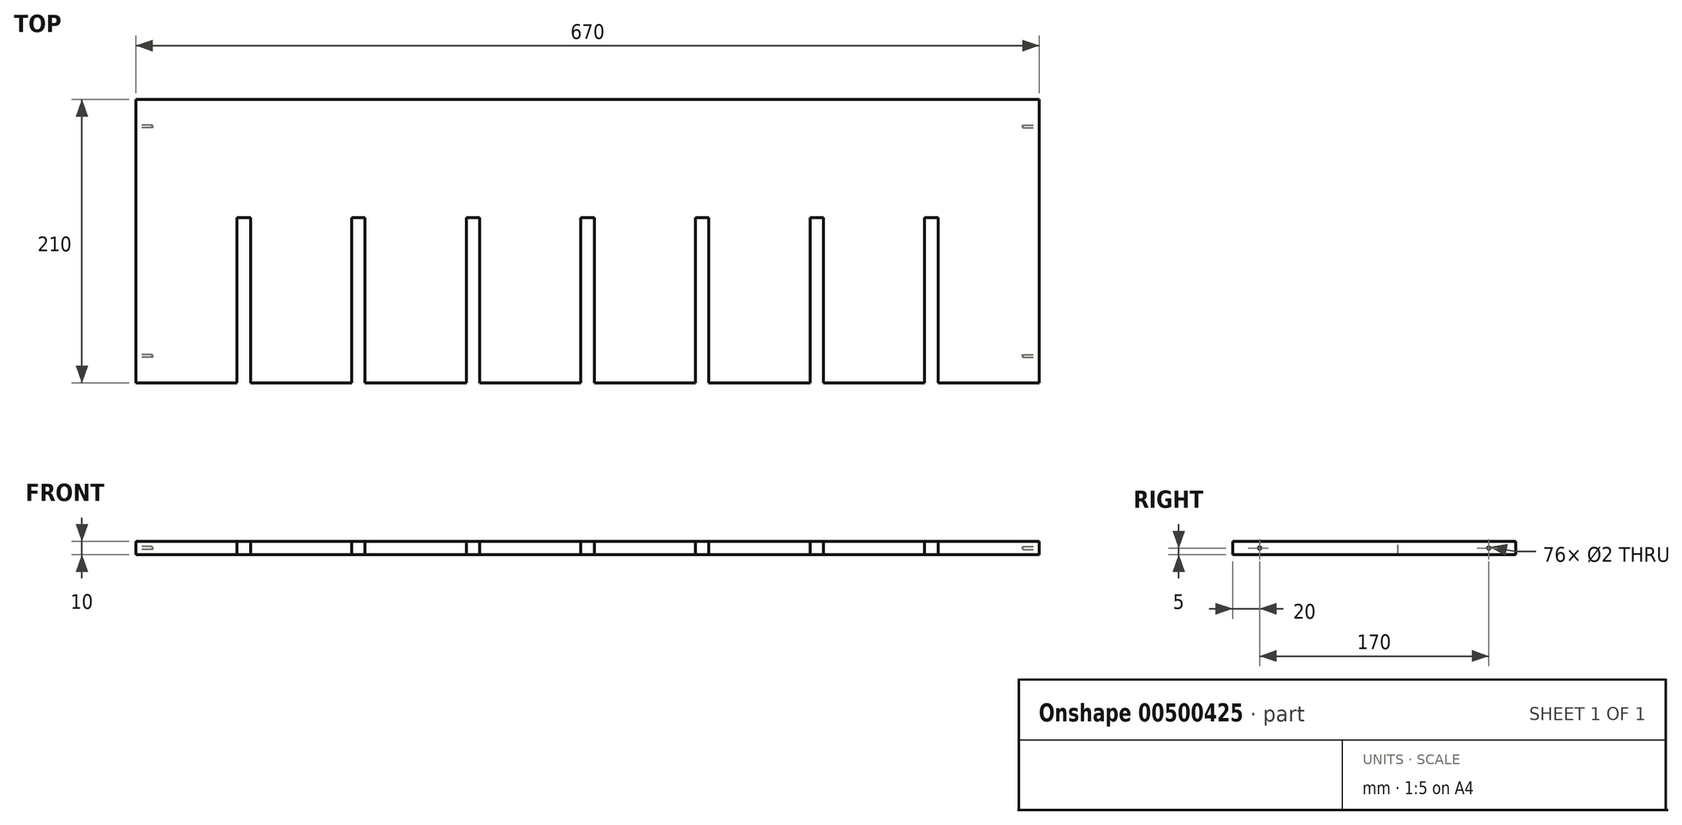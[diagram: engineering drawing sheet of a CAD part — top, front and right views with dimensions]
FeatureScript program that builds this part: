
annotation { "Feature Type Name" : "Feature", "Feature Type Description" : "" }
export const myFeature = defineFeature(function(context is Context, id is Id, definition is map)
    precondition{}
    {
        {
            var Q0;
            Q0=qCreatedBy(makeId("Top.planeOp"),FACE);
            var sketch = newSketch(context, id + "F0", { "sketchPlane" : qUnion([Q0])});
            skLineSegment(sketch, "E0.bottom", {"start": v(0, 0) * mm, "end": v(-670, 0) * mm});
            skLineSegment(sketch, "E0.top", {"start": v(0, 210) * mm, "end": v(-670, 210) * mm});
            skLineSegment(sketch, "E0.left", {"start": v(0, 0) * mm, "end": v(0, 210) * mm});
            skLineSegment(sketch, "E0.right", {"start": v(-670, 0) * mm, "end": v(-670, 210) * mm});
            skSolve(sketch);
        }
        {
            var Q0;
            Q0 = qSketchRegion(id + "F0", true);
            extrude(context, id + "F1", {"entities" : qUnion([Q0]), "depth" : 10 * mm});
        }
        {
            var Q0;
            Q0=makeQuery(id+"F1.opExtrude","CAP_FACE",FACE,{"disambiguationData":[OSD([sQuery(id+"F0.wireOp",EDGE,"E0.bottom"),sQuery(id+"F0.wireOp",EDGE,"E0.top"),sQuery(id+"F0.wireOp",EDGE,"E0.left"),sQuery(id+"F0.wireOp",EDGE,"E0.right")])],"isStart":false});
            var sketch = newSketch(context, id + "F2", { "sketchPlane" : qUnion([Q0])});
            skPoint(sketch, "E1", {"position": v(-595, 122.53) * mm});
            skPoint(sketch, "E2", {"position": v(-585, 122.53) * mm});
            skPoint(sketch, "E3", {"position": v(-510, 122.53) * mm});
            skPoint(sketch, "E4", {"position": v(-500, 122.53) * mm});
            skPoint(sketch, "E5", {"position": v(-425, 122.53) * mm});
            skPoint(sketch, "E6", {"position": v(-85, 122.53) * mm});
            skPoint(sketch, "E7", {"position": v(-75, 122.53) * mm});
            skPoint(sketch, "E8", {"position": v(-415, 122.53) * mm});
            skPoint(sketch, "E9", {"position": v(-340, 122.53) * mm});
            skPoint(sketch, "E10", {"position": v(-330, 122.53) * mm});
            skPoint(sketch, "E11", {"position": v(-255, 122.53) * mm});
            skPoint(sketch, "E12", {"position": v(-245, 122.53) * mm});
            skPoint(sketch, "E13", {"position": v(-170, 122.53) * mm});
            skPoint(sketch, "E14", {"position": v(-160, 122.53) * mm});
            skLineSegment(sketch, "E15.bottom", {"start": v(-595, 122.53) * mm, "end": v(-585, 122.53) * mm});
            skLineSegment(sketch, "E15.top", {"start": v(-595, 0) * mm, "end": v(-585, 0) * mm});
            skLineSegment(sketch, "E15.left", {"start": v(-595, 122.53) * mm, "end": v(-595, 0) * mm});
            skLineSegment(sketch, "E15.right", {"start": v(-585, 122.53) * mm, "end": v(-585, 0) * mm});
            skLineSegment(sketch, "E16.bottom", {"start": v(-510, 122.53) * mm, "end": v(-500, 122.53) * mm});
            skLineSegment(sketch, "E16.top", {"start": v(-510, 0) * mm, "end": v(-500, 0) * mm});
            skLineSegment(sketch, "E16.left", {"start": v(-510, 122.53) * mm, "end": v(-510, 0) * mm});
            skLineSegment(sketch, "E16.right", {"start": v(-500, 122.53) * mm, "end": v(-500, 0) * mm});
            skLineSegment(sketch, "E17.bottom", {"start": v(-425, 122.53) * mm, "end": v(-415, 122.53) * mm});
            skLineSegment(sketch, "E17.top", {"start": v(-425, 0) * mm, "end": v(-415, 0) * mm});
            skLineSegment(sketch, "E17.left", {"start": v(-425, 122.53) * mm, "end": v(-425, 0) * mm});
            skLineSegment(sketch, "E17.right", {"start": v(-415, 122.53) * mm, "end": v(-415, 0) * mm});
            skLineSegment(sketch, "E18.bottom", {"start": v(-340, 122.53) * mm, "end": v(-330, 122.53) * mm});
            skLineSegment(sketch, "E18.top", {"start": v(-340, 0) * mm, "end": v(-330, 0) * mm});
            skLineSegment(sketch, "E18.left", {"start": v(-340, 122.53) * mm, "end": v(-340, 0) * mm});
            skLineSegment(sketch, "E18.right", {"start": v(-330, 122.53) * mm, "end": v(-330, 0) * mm});
            skLineSegment(sketch, "E19.bottom", {"start": v(-255, 122.53) * mm, "end": v(-245, 122.53) * mm});
            skLineSegment(sketch, "E19.top", {"start": v(-255, 0) * mm, "end": v(-245, 0) * mm});
            skLineSegment(sketch, "E19.left", {"start": v(-255, 122.53) * mm, "end": v(-255, 0) * mm});
            skLineSegment(sketch, "E19.right", {"start": v(-245, 122.53) * mm, "end": v(-245, 0) * mm});
            skLineSegment(sketch, "E20.bottom", {"start": v(-170, 122.53) * mm, "end": v(-160, 122.53) * mm});
            skLineSegment(sketch, "E20.top", {"start": v(-170, 0) * mm, "end": v(-160, 0) * mm});
            skLineSegment(sketch, "E20.left", {"start": v(-170, 122.53) * mm, "end": v(-170, 0) * mm});
            skLineSegment(sketch, "E20.right", {"start": v(-160, 122.53) * mm, "end": v(-160, 0) * mm});
            skLineSegment(sketch, "E21.bottom", {"start": v(-85, 122.53) * mm, "end": v(-75, 122.53) * mm});
            skLineSegment(sketch, "E21.top", {"start": v(-85, 0) * mm, "end": v(-75, 0) * mm});
            skLineSegment(sketch, "E21.left", {"start": v(-85, 122.53) * mm, "end": v(-85, 0) * mm});
            skLineSegment(sketch, "E21.right", {"start": v(-75, 122.53) * mm, "end": v(-75, 0) * mm});
            skSolve(sketch);
        }
        {
            var Q0;
            Q0=makeQuery(id+"F2.imprint","IMPRINT",FACE,{"disambiguationData":[TD([[makeQuery(id+"F2.imprint","IMPRINT",EDGE,{"derivedFrom":sQuery(id+"F2.wireOp",EDGE,"E15.bottom")}),-1.0]])]});
            var Q1;
            Q1=makeQuery(id+"F2.imprint","IMPRINT",FACE,{"disambiguationData":[TD([[makeQuery(id+"F2.imprint","IMPRINT",EDGE,{"derivedFrom":sQuery(id+"F2.wireOp",EDGE,"E16.bottom")}),-1.0]])]});
            var Q2;
            Q2=makeQuery(id+"F2.imprint","IMPRINT",FACE,{"disambiguationData":[TD([[makeQuery(id+"F2.imprint","IMPRINT",EDGE,{"derivedFrom":sQuery(id+"F2.wireOp",EDGE,"E17.bottom")}),-1.0]])]});
            var Q3;
            Q3=makeQuery(id+"F2.imprint","IMPRINT",FACE,{"disambiguationData":[TD([[makeQuery(id+"F2.imprint","IMPRINT",EDGE,{"derivedFrom":sQuery(id+"F2.wireOp",EDGE,"E18.bottom")}),-1.0]])]});
            var Q4;
            Q4=makeQuery(id+"F2.imprint","IMPRINT",FACE,{"disambiguationData":[TD([[makeQuery(id+"F2.imprint","IMPRINT",EDGE,{"derivedFrom":sQuery(id+"F2.wireOp",EDGE,"E19.bottom")}),-1.0]])]});
            var Q5;
            Q5=makeQuery(id+"F2.imprint","IMPRINT",FACE,{"disambiguationData":[TD([[makeQuery(id+"F2.imprint","IMPRINT",EDGE,{"derivedFrom":sQuery(id+"F2.wireOp",EDGE,"E20.bottom")}),-1.0]])]});
            var Q6;
            Q6=makeQuery(id+"F2.imprint","IMPRINT",FACE,{"disambiguationData":[TD([[makeQuery(id+"F2.imprint","IMPRINT",EDGE,{"derivedFrom":sQuery(id+"F2.wireOp",EDGE,"E21.bottom")}),-1.0]])]});
            extrude(context, id + "F3", {"entities" : qUnion([Q0, Q1, Q2, Q3, Q4, Q5, Q6]), "operationType" : NewBodyOperationType.REMOVE, "oppositeDirection" : true, "depth" : 25 * mm});
        }
        {
            var Q0;
            Q0=makeQuery(id+"F1.opExtrude","SWEPT_FACE",FACE,{"disambiguationData":[OSD([sQuery(id+"F0.wireOp",EDGE,"E0.right")])]});
            var sketch = newSketch(context, id + "F4", { "sketchPlane" : qUnion([Q0])});
            skPoint(sketch, "E22", {"position": v(-190, 5) * mm});
            skPoint(sketch, "E22.positionSnap0", {"position": v(-210, 5) * mm});
            skPoint(sketch, "E23", {"position": v(-20, 5) * mm});
            skSolve(sketch);
        }
        {
            var Q0;
            Q0=sQuery(id+"F4.wireOp",VERTEX,"E22");
            var Q1;
            Q1=sQuery(id+"F4.wireOp",VERTEX,"E23");
            var Q2;
            Q2=makeQuery(id+"F1.opExtrude","SWEPT_BODY",BODY,{"disambiguationData":[OSD([sQuery(id+"F0.wireOp",EDGE,"E0.bottom"),sQuery(id+"F0.wireOp",EDGE,"E0.top"),sQuery(id+"F0.wireOp",EDGE,"E0.left"),sQuery(id+"F0.wireOp",EDGE,"E0.right")])]});
            hole(context, id + "F5", {"style" : HoleStyle.SIMPLE, "endStyle" : HoleEndStyle.BLIND, "holeDiameter" : 2 * mm, "holeDepth" : 12 * mm, "isTappedThrough" : true, "tappedDepth" : 12 * mm, "tapClearance" : 3, "locations" : qUnion([Q0, Q1]), "scope" : qUnion([Q2])});
        }
        {
            var Q0;
            Q0=makeQuery(id+"F1.opExtrude","SWEPT_FACE",FACE,{"disambiguationData":[OSD([sQuery(id+"F0.wireOp",EDGE,"E0.left")])]});
            var sketch = newSketch(context, id + "F6", { "sketchPlane" : qUnion([Q0])});
            skPoint(sketch, "E24", {"position": v(20, 5) * mm});
            skPoint(sketch, "E24.positionSnap0", {"position": v(0, 5) * mm});
            skPoint(sketch, "E25", {"position": v(190, 5) * mm});
            skSolve(sketch);
        }
        {
            var Q0;
            Q0=sQuery(id+"F6.wireOp",VERTEX,"E24");
            var Q1;
            Q1=sQuery(id+"F6.wireOp",VERTEX,"E25");
            var Q2;
            Q2=makeQuery(id+"F1.opExtrude","SWEPT_BODY",BODY,{"disambiguationData":[OSD([sQuery(id+"F0.wireOp",EDGE,"E0.bottom"),sQuery(id+"F0.wireOp",EDGE,"E0.top"),sQuery(id+"F0.wireOp",EDGE,"E0.left"),sQuery(id+"F0.wireOp",EDGE,"E0.right")])]});
            hole(context, id + "F7", {"style" : HoleStyle.SIMPLE, "endStyle" : HoleEndStyle.BLIND, "holeDiameter" : 2 * mm, "holeDepth" : 12 * mm, "isTappedThrough" : true, "tappedDepth" : 12 * mm, "tapClearance" : 3, "locations" : qUnion([Q0, Q1]), "scope" : qUnion([Q2])});
        }
    });
